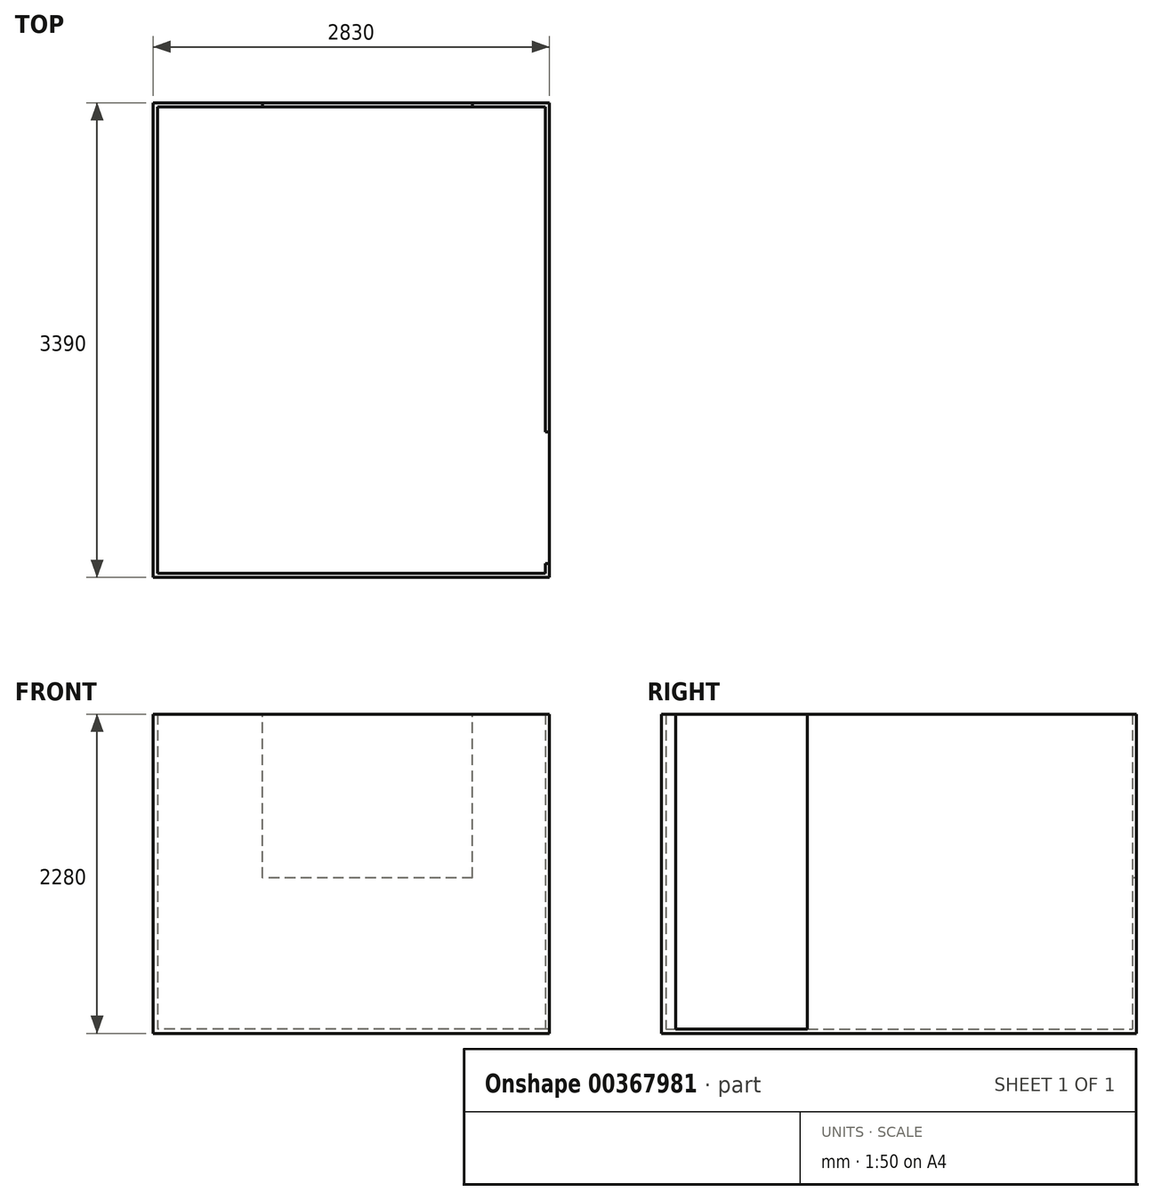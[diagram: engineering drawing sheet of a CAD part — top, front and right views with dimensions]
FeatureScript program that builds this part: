
annotation { "Feature Type Name" : "Feature", "Feature Type Description" : "" }
export const myFeature = defineFeature(function(context is Context, id is Id, definition is map)
    precondition{}
    {
        {
            var Q0;
            Q0=qCreatedBy(makeId("Top.planeOp"),FACE);
            var sketch = newSketch(context, id + "F0", { "sketchPlane" : qUnion([Q0])});
            skLineSegment(sketch, "E0.bottom", {"start": v(0, 0) * mm, "end": v(-2770, 0) * mm});
            skLineSegment(sketch, "E0.top", {"start": v(0, 3330) * mm, "end": v(-2770, 3330) * mm});
            skLineSegment(sketch, "E0.left", {"start": v(0, 0) * mm, "end": v(0, 70) * mm});
            skLineSegment(sketch, "E0.right", {"start": v(-2770, 0) * mm, "end": v(-2770, 3330) * mm});
            skLineSegment(sketch, "E1.0", {"start": v(-2800, -30) * mm, "end": v(-2800, 3360) * mm});
            skLineSegment(sketch, "E1.1", {"start": v(30, -30) * mm, "end": v(-2800, -30) * mm});
            skLineSegment(sketch, "E1.2", {"start": v(30, -30) * mm, "end": v(30, 70) * mm});
            skLineSegment(sketch, "E1.3", {"start": v(30, 3360) * mm, "end": v(-2800, 3360) * mm});
            skLineSegment(sketch, "E2", {"start": v(30, 1010) * mm, "end": v(0, 1010) * mm});
            skLineSegment(sketch, "E3", {"start": v(30, 70) * mm, "end": v(0, 70) * mm});
            skLineSegment(sketch, "E4.trimOffspring", {"start": v(0, 1010) * mm, "end": v(0, 3330) * mm});
            skLineSegment(sketch, "E5.trimOffspring", {"start": v(30, 1010) * mm, "end": v(30, 3360) * mm});
            skSolve(sketch);
        }
        {
            var Q0;
            Q0=makeQuery(id+"F0.imprint","IMPRINT",FACE,{"disambiguationData":[TD([[makeQuery(id+"F0.imprint","IMPRINT",EDGE,{"derivedFrom":sQuery(id+"F0.wireOp",EDGE,"E0.bottom")}),1.0]])]});
            extrude(context, id + "F1", {"entities" : qUnion([Q0]), "depth" : 2250 * mm});
        }
        {
            var Q0;
            Q0=qCreatedBy(makeId("Top.planeOp"),FACE);
            var sketch = newSketch(context, id + "F2", { "sketchPlane" : qUnion([Q0])});
            skLineSegment(sketch, "E6.bottom", {"start": v(-2800, -30) * mm, "end": v(30, -30) * mm});
            skLineSegment(sketch, "E6.top", {"start": v(-2800, 3360) * mm, "end": v(30, 3360) * mm});
            skLineSegment(sketch, "E6.left", {"start": v(-2800, -30) * mm, "end": v(-2800, 3360) * mm});
            skLineSegment(sketch, "E6.right", {"start": v(30, -30) * mm, "end": v(30, 3360) * mm});
            skSolve(sketch);
        }
        {
            var Q0;
            Q0=makeQuery(id+"F2.imprint","IMPRINT",FACE,{"disambiguationData":[TD([[makeQuery(id+"F2.imprint","IMPRINT",EDGE,{"derivedFrom":sQuery(id+"F2.wireOp",EDGE,"E6.bottom")}),1.0]])]});
            extrude(context, id + "F3", {"entities" : qUnion([Q0]), "operationType" : NewBodyOperationType.ADD, "oppositeDirection" : true, "depth" : 30 * mm});
        }
        {
            var Q0;
            Q0=makeQuery(id+"F1.opExtrude","SWEPT_FACE",FACE,{"disambiguationData":[OSD([sQuery(id+"F0.wireOp",EDGE,"E0.top")])]});
            var sketch = newSketch(context, id + "F4", { "sketchPlane" : qUnion([Q0])});
            skLineSegment(sketch, "E7.bottom", {"start": v(-2020, 2250) * mm, "end": v(-520, 2250) * mm});
            skLineSegment(sketch, "E7.top", {"start": v(-2020, 1080) * mm, "end": v(-520, 1080) * mm});
            skLineSegment(sketch, "E7.left", {"start": v(-2020, 2250) * mm, "end": v(-2020, 1080) * mm});
            skLineSegment(sketch, "E7.right", {"start": v(-520, 2250) * mm, "end": v(-520, 1080) * mm});
            skSolve(sketch);
        }
        {
            var Q0;
            Q0=makeQuery(id+"F4.imprint","IMPRINT",FACE,{"disambiguationData":[TD([[makeQuery(id+"F4.imprint","IMPRINT",EDGE,{"derivedFrom":sQuery(id+"F4.wireOp",EDGE,"E7.bottom")}),1.0]])]});
            extrude(context, id + "F5", {"entities" : qUnion([Q0]), "operationType" : NewBodyOperationType.REMOVE, "endBound" : BoundingType.UP_TO_NEXT, "oppositeDirection" : true, "depth" : 25 * mm});
        }
    });
